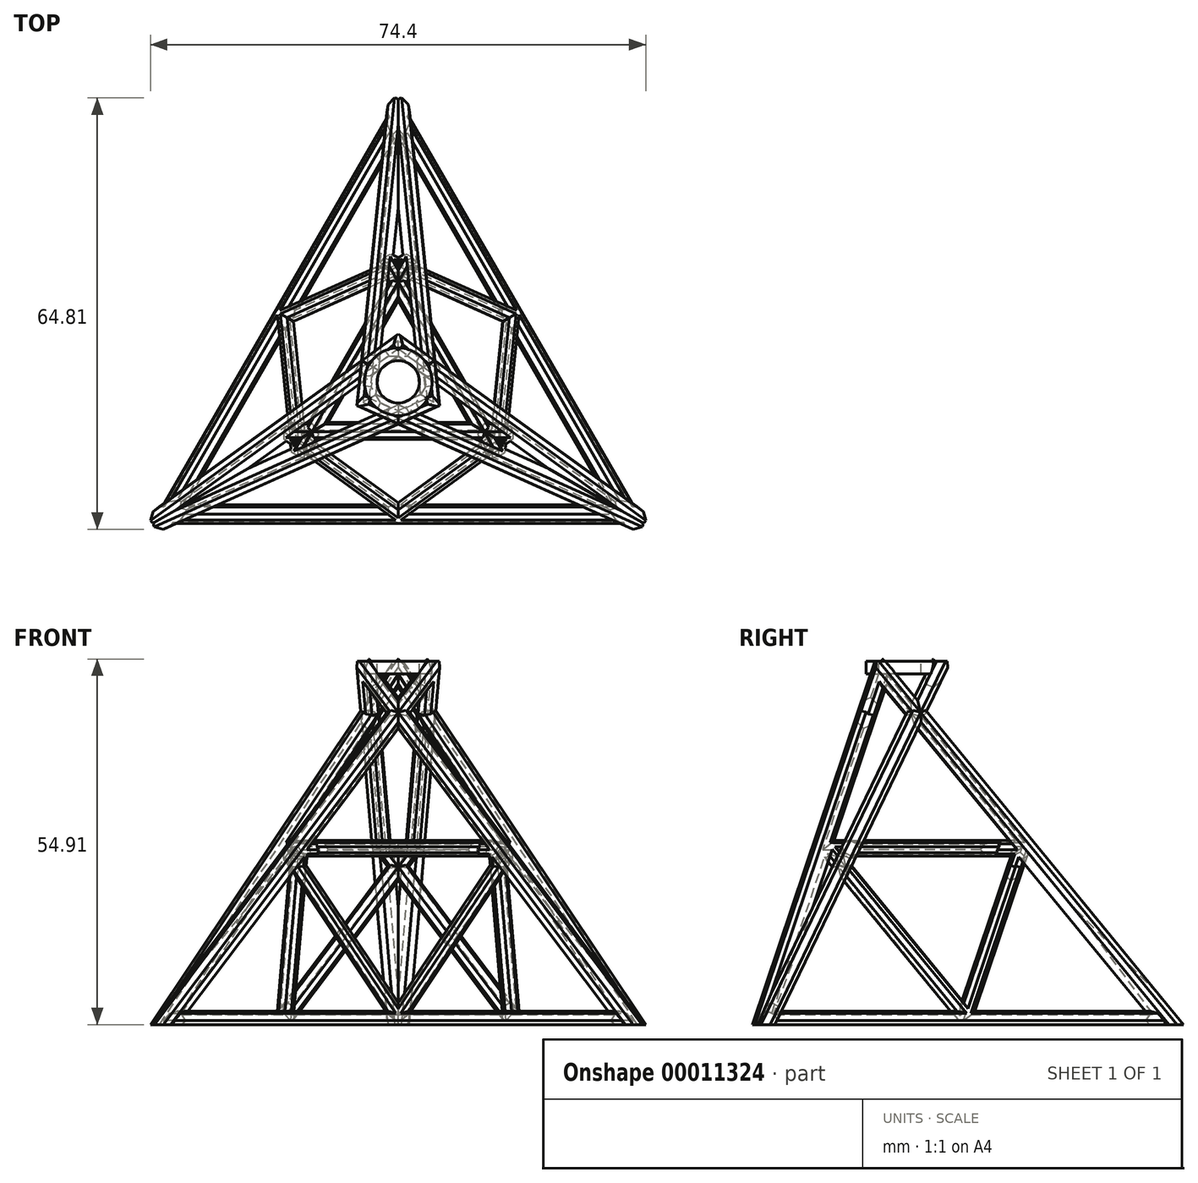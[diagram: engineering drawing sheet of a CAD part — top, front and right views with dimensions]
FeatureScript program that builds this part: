
annotation { "Feature Type Name" : "Feature", "Feature Type Description" : "" }
export const myFeature = defineFeature(function(context is Context, id is Id, definition is map)
    precondition{}
    {
        {
            var Q0;
            Q0=qCreatedBy(makeId("Top.planeOp"),FACE);
            cPlane(context, id + "F0", {"entities" : qUnion([Q0]), "cplaneType" : CPlaneType.OFFSET, "offset" : 38.1 * mm, "width" : 152.4 * mm, "height" : 152.4 * mm});
        }
        {
            var Q0;
            Q0=qCreatedBy(makeId("Front.planeOp"),FACE);
            var sketch = newSketch(context, id + "F1", { "sketchPlane" : qUnion([Q0])});
            skLineSegment(sketch, "E0", {"start": v(0, 0) * mm, "end": v(0, 46.8) * mm, "construction": true});
            skSolve(sketch);
        }
        {
            var Q0;
            Q0=qCreatedBy(id+"F0.planeOp",FACE);
            var sketch = newSketch(context, id + "F2", { "sketchPlane" : qUnion([Q0])});
            skCircle(sketch, "E1", {"center": v(0, 0) * mm, "radius": 3.18 * mm, "construction": true});
            skPoint(sketch, "E2", {"position": v(0, -3.18) * mm});
            skPoint(sketch, "E3.1.0", {"position": v(2.75, -1.59) * mm});
            skPoint(sketch, "E3.2.0", {"position": v(2.75, 1.59) * mm});
            skPoint(sketch, "E3.3.0", {"position": v(0, 3.18) * mm});
            skPoint(sketch, "E3.4.0", {"position": v(-2.75, 1.59) * mm});
            skPoint(sketch, "E3.5.0", {"position": v(-2.75, -1.59) * mm});
            skSolve(sketch);
        }
        {
            var Q0;
            Q0=qCreatedBy(makeId("Top.planeOp"),FACE);
            var sketch = newSketch(context, id + "F3", { "sketchPlane" : qUnion([Q0])});
            skCircle(sketch, "E4", {"center": v(0, 0) * mm, "radius": 21.59 * mm, "construction": true});
            skLineSegment(sketch, "E5", {"start": v(37.4, -21.6) * mm, "end": v(-37.4, -21.59) * mm});
            skLineSegment(sketch, "E6", {"start": v(-37.4, -21.59) * mm, "end": v(0, 43.18) * mm});
            skLineSegment(sketch, "E7", {"start": v(0, 43.18) * mm, "end": v(37.4, -21.6) * mm});
            skPoint(sketch, "E8", {"position": v(0, -21.59) * mm});
            skPoint(sketch, "E9", {"position": v(-18.7, 10.8) * mm});
            skCircle(sketch, "E10", {"center": v(0, 0) * mm, "radius": 38.1 * mm, "construction": true});
            skSolve(sketch);
        }
        {
            var Q0;
            Q0=sQuery(id+"F2.wireOp",VERTEX,"E2");
            var Q1;
            Q1=sQuery(id+"F3.wireOp",VERTEX,"E5.end");
            var Q2;
            Q2=sQuery(id+"F3.wireOp",VERTEX,"E5.start");
            cPlane(context, id + "F4", {"entities" : qUnion([Q0, Q1, Q2]), "cplaneType" : CPlaneType.THREE_POINT, "offset" : 152.4 * mm, "width" : 152.4 * mm, "height" : 152.4 * mm});
        }
        {
            var Q0;
            Q0=qCreatedBy(id+"F4.planeOp",FACE);
            var sketch = newSketch(context, id + "F5", { "sketchPlane" : qUnion([Q0])});
            skPoint(sketch, "E11.0", {"position": v(37.4, -9.4) * mm});
            skPoint(sketch, "E12.0", {"position": v(-37.4, -9.4) * mm});
            skLineSegment(sketch, "E13", {"start": v(37.4, -9.4) * mm, "end": v(0, 52.7) * mm});
            skLineSegment(sketch, "E14", {"start": v(0, 52.7) * mm, "end": v(-37.4, -9.4) * mm});
            skLineSegment(sketch, "E15.0", {"start": v(-37.4, -9.4) * mm, "end": v(37.4, -9.4) * mm});
            skPoint(sketch, "E16", {"position": v(-18.7, 21.65) * mm});
            skPoint(sketch, "E17", {"position": v(18.7, 21.65) * mm});
            skLineSegment(sketch, "E18", {"start": v(-18.7, 21.65) * mm, "end": v(18.7, 21.65) * mm});
            skLineSegment(sketch, "E19", {"start": v(-18.7, 21.65) * mm, "end": v(0, -9.4) * mm});
            skLineSegment(sketch, "E20", {"start": v(0, -9.4) * mm, "end": v(18.7, 21.65) * mm});
            skLineSegment(sketch, "E21.0", {"start": v(32.9, -6.86) * mm, "end": v(0, 47.78) * mm});
            skLineSegment(sketch, "E21.1", {"start": v(-32.9, -6.86) * mm, "end": v(32.9, -6.86) * mm});
            skLineSegment(sketch, "E21.2", {"start": v(0, 47.78) * mm, "end": v(-32.9, -6.86) * mm});
            skLineSegment(sketch, "E22.0", {"start": v(-15.1, 19.62) * mm, "end": v(15.1, 19.62) * mm});
            skLineSegment(sketch, "E22.1", {"start": v(-15.1, 19.62) * mm, "end": v(0, -5.46) * mm});
            skLineSegment(sketch, "E22.2", {"start": v(0, -5.46) * mm, "end": v(15.1, 19.62) * mm});
            skSolve(sketch);
        }
        {
            var Q0;
            {var subQ0=sQuery(id+"F5.wireOp",EDGE,"E21.1");var subQ3=sQuery(id+"F5.wireOp",EDGE,"E21.0");var subQ4=makeQuery(id+"F5.imprint","INTERSECT",VERTEX,{"derivedFrom":[subQ3,subQ0]});Q0=makeQuery(id+"F5.imprint","IMPRINT",FACE,{"disambiguationData":[TD([[makeQuery(id+"F5.imprint","IMPRINT",EDGE,{"disambiguationData":[TD([[subQ4,-1.0]])],"derivedFrom":subQ3}),-1.0]])]});}
            var Q1;
            {var subQ0=sQuery(id+"F5.wireOp",EDGE,"E21.2");var subQ3=sQuery(id+"F5.wireOp",EDGE,"E21.1");var subQ4=makeQuery(id+"F5.imprint","INTERSECT",VERTEX,{"derivedFrom":[subQ3,subQ0]});Q1=makeQuery(id+"F5.imprint","IMPRINT",FACE,{"disambiguationData":[TD([[makeQuery(id+"F5.imprint","IMPRINT",EDGE,{"disambiguationData":[TD([[subQ4,-1.0]])],"derivedFrom":subQ3}),-1.0]])]});}
            var Q2;
            {var subQ0=sQuery(id+"F5.wireOp",EDGE,"E21.0");var subQ3=sQuery(id+"F5.wireOp",EDGE,"E18");var subQ4=makeQuery(id+"F5.imprint","INTERSECT",VERTEX,{"derivedFrom":[subQ3,subQ0]});Q2=makeQuery(id+"F5.imprint","IMPRINT",FACE,{"disambiguationData":[TD([[makeQuery(id+"F5.imprint","IMPRINT",EDGE,{"disambiguationData":[TD([[subQ4,1.0]])],"derivedFrom":subQ0}),-1.0]])]});}
            var Q3;
            {var subQ0=sQuery(id+"F5.wireOp",EDGE,"E21.1");var subQ3=sQuery(id+"F5.wireOp",EDGE,"E19");var subQ4=makeQuery(id+"F5.imprint","INTERSECT",VERTEX,{"derivedFrom":[subQ3,subQ0]});Q3=makeQuery(id+"F5.imprint","IMPRINT",FACE,{"disambiguationData":[TD([[makeQuery(id+"F5.imprint","IMPRINT",EDGE,{"disambiguationData":[TD([[subQ4,-1.0]])],"derivedFrom":subQ0}),-1.0]])]});}
            var Q4;
            Q4=makeQuery(id+"F5.imprint","IMPRINT",FACE,{"disambiguationData":[TD([[makeQuery(id+"F5.imprint","IMPRINT",EDGE,{"derivedFrom":sQuery(id+"F5.wireOp",EDGE,"E22.0")}),1.0]])]});
            var Q5;
            {var subQ0=sQuery(id+"F5.wireOp",EDGE,"E21.2");var subQ3=sQuery(id+"F5.wireOp",EDGE,"E21.0");var subQ4=makeQuery(id+"F5.imprint","INTERSECT",VERTEX,{"derivedFrom":[subQ3,subQ0]});Q5=makeQuery(id+"F5.imprint","IMPRINT",FACE,{"disambiguationData":[TD([[makeQuery(id+"F5.imprint","IMPRINT",EDGE,{"disambiguationData":[TD([[subQ4,1.0]])],"derivedFrom":subQ3}),-1.0]])]});}
            var Q6;
            {var subQ0=sQuery(id+"F5.wireOp",EDGE,"E21.2");var subQ3=sQuery(id+"F5.wireOp",EDGE,"E18");var subQ4=makeQuery(id+"F5.imprint","INTERSECT",VERTEX,{"derivedFrom":[subQ3,subQ0]});Q6=makeQuery(id+"F5.imprint","IMPRINT",FACE,{"disambiguationData":[TD([[makeQuery(id+"F5.imprint","IMPRINT",EDGE,{"disambiguationData":[TD([[subQ4,-1.0]])],"derivedFrom":subQ0}),-1.0]])]});}
            extrude(context, id + "F6", {"entities" : qUnion([Q0, Q1, Q2, Q3, Q4, Q5, Q6]), "depth" : 2.54 * mm});
        }
        {
            var Q0;
            Q0=makeQuery(id+"F6.opExtrude","CAP_EDGE",EDGE,{"disambiguationData":[OSD([sQuery(id+"F5.wireOp",EDGE,"E13")])],"isStart":true});
            var Q1;
            Q1=makeQuery(id+"F6.opExtrude","CAP_EDGE",EDGE,{"disambiguationData":[OSD([sQuery(id+"F5.wireOp",EDGE,"E14")])],"isStart":true});
            var Q2;
            Q2=makeQuery(id+"F6.opExtrude","CAP_EDGE",EDGE,{"disambiguationData":[OSD([sQuery(id+"F5.wireOp",EDGE,"E14")])],"isStart":false});
            var Q3;
            Q3=makeQuery(id+"F6.opExtrude","CAP_EDGE",EDGE,{"disambiguationData":[OSD([sQuery(id+"F5.wireOp",EDGE,"E13")])],"isStart":false});
            var Q4;
            {var subQ0=sQuery(id+"F5.wireOp",EDGE,"E21.0");Q4=makeQuery(id+"F6.opExtrude","CAP_EDGE",EDGE,{"disambiguationData":[OSD([subQ0]),TDD([makeQuery(id+"F5.imprint","IMPRINT",EDGE,{"disambiguationData":[TD([[makeQuery(id+"F5.imprint","INTERSECT",VERTEX,{"derivedFrom":[subQ0,sQuery(id+"F5.wireOp",EDGE,"E21.2")]}),1.0]])],"derivedFrom":subQ0})])],"isStart":true});}
            var Q5;
            {var subQ0=sQuery(id+"F5.wireOp",EDGE,"E21.0");Q5=makeQuery(id+"F6.opExtrude","CAP_EDGE",EDGE,{"disambiguationData":[OSD([subQ0]),TDD([makeQuery(id+"F5.imprint","IMPRINT",EDGE,{"disambiguationData":[TD([[makeQuery(id+"F5.imprint","INTERSECT",VERTEX,{"derivedFrom":[subQ0,sQuery(id+"F5.wireOp",EDGE,"E21.2")]}),1.0]])],"derivedFrom":subQ0})])],"isStart":false});}
            var Q6;
            {var subQ0=sQuery(id+"F5.wireOp",EDGE,"E21.2");Q6=makeQuery(id+"F6.opExtrude","CAP_EDGE",EDGE,{"disambiguationData":[OSD([subQ0]),TDD([makeQuery(id+"F5.imprint","IMPRINT",EDGE,{"disambiguationData":[TD([[makeQuery(id+"F5.imprint","INTERSECT",VERTEX,{"derivedFrom":[sQuery(id+"F5.wireOp",EDGE,"E21.0"),subQ0]}),-1.0]])],"derivedFrom":subQ0})])],"isStart":true});}
            var Q7;
            {var subQ0=sQuery(id+"F5.wireOp",EDGE,"E21.2");Q7=makeQuery(id+"F6.opExtrude","CAP_EDGE",EDGE,{"disambiguationData":[OSD([subQ0]),TDD([makeQuery(id+"F5.imprint","IMPRINT",EDGE,{"disambiguationData":[TD([[makeQuery(id+"F5.imprint","INTERSECT",VERTEX,{"derivedFrom":[sQuery(id+"F5.wireOp",EDGE,"E21.0"),subQ0]}),-1.0]])],"derivedFrom":subQ0})])],"isStart":false});}
            var Q8;
            Q8=makeQuery(id+"F6.opExtrude","CAP_EDGE",EDGE,{"disambiguationData":[OSD([sQuery(id+"F5.wireOp",EDGE,"E18")])],"isStart":true});
            var Q9;
            Q9=makeQuery(id+"F6.opExtrude","CAP_EDGE",EDGE,{"disambiguationData":[OSD([sQuery(id+"F5.wireOp",EDGE,"E18")])],"isStart":false});
            var Q10;
            Q10=makeQuery(id+"F6.opExtrude","CAP_EDGE",EDGE,{"disambiguationData":[OSD([sQuery(id+"F5.wireOp",EDGE,"E22.0")])],"isStart":true});
            var Q11;
            Q11=makeQuery(id+"F6.opExtrude","CAP_EDGE",EDGE,{"disambiguationData":[OSD([sQuery(id+"F5.wireOp",EDGE,"E22.0")])],"isStart":false});
            var Q12;
            Q12=makeQuery(id+"F6.opExtrude","CAP_EDGE",EDGE,{"disambiguationData":[OSD([sQuery(id+"F5.wireOp",EDGE,"E22.2")])],"isStart":true});
            var Q13;
            Q13=makeQuery(id+"F6.opExtrude","CAP_EDGE",EDGE,{"disambiguationData":[OSD([sQuery(id+"F5.wireOp",EDGE,"E22.2")])],"isStart":false});
            var Q14;
            Q14=makeQuery(id+"F6.opExtrude","CAP_EDGE",EDGE,{"disambiguationData":[OSD([sQuery(id+"F5.wireOp",EDGE,"E22.1")])],"isStart":true});
            var Q15;
            Q15=makeQuery(id+"F6.opExtrude","CAP_EDGE",EDGE,{"disambiguationData":[OSD([sQuery(id+"F5.wireOp",EDGE,"E19")])],"isStart":true});
            var Q16;
            Q16=makeQuery(id+"F6.opExtrude","CAP_EDGE",EDGE,{"disambiguationData":[OSD([sQuery(id+"F5.wireOp",EDGE,"E19")])],"isStart":false});
            var Q17;
            Q17=makeQuery(id+"F6.opExtrude","CAP_EDGE",EDGE,{"disambiguationData":[OSD([sQuery(id+"F5.wireOp",EDGE,"E22.1")])],"isStart":false});
            var Q18;
            Q18=makeQuery(id+"F6.opExtrude","CAP_EDGE",EDGE,{"disambiguationData":[OSD([sQuery(id+"F5.wireOp",EDGE,"E20")])],"isStart":false});
            var Q19;
            Q19=makeQuery(id+"F6.opExtrude","CAP_EDGE",EDGE,{"disambiguationData":[OSD([sQuery(id+"F5.wireOp",EDGE,"E20")])],"isStart":true});
            var Q20;
            {var subQ0=sQuery(id+"F5.wireOp",EDGE,"E21.1");Q20=makeQuery(id+"F6.opExtrude","CAP_EDGE",EDGE,{"disambiguationData":[OSD([subQ0]),TDD([makeQuery(id+"F5.imprint","IMPRINT",EDGE,{"disambiguationData":[TD([[makeQuery(id+"F5.imprint","INTERSECT",VERTEX,{"derivedFrom":[sQuery(id+"F5.wireOp",EDGE,"E21.0"),subQ0]}),1.0]])],"derivedFrom":subQ0})])],"isStart":false});}
            var Q21;
            {var subQ0=sQuery(id+"F5.wireOp",EDGE,"E21.1");Q21=makeQuery(id+"F6.opExtrude","CAP_EDGE",EDGE,{"disambiguationData":[OSD([subQ0]),TDD([makeQuery(id+"F5.imprint","IMPRINT",EDGE,{"disambiguationData":[TD([[makeQuery(id+"F5.imprint","INTERSECT",VERTEX,{"derivedFrom":[sQuery(id+"F5.wireOp",EDGE,"E21.0"),subQ0]}),1.0]])],"derivedFrom":subQ0})])],"isStart":true});}
            var Q22;
            {var subQ0=sQuery(id+"F5.wireOp",EDGE,"E21.1");Q22=makeQuery(id+"F6.opExtrude","CAP_EDGE",EDGE,{"disambiguationData":[OSD([subQ0]),TDD([makeQuery(id+"F5.imprint","IMPRINT",EDGE,{"disambiguationData":[TD([[makeQuery(id+"F5.imprint","INTERSECT",VERTEX,{"derivedFrom":[subQ0,sQuery(id+"F5.wireOp",EDGE,"E21.2")]}),-1.0]])],"derivedFrom":subQ0})])],"isStart":false});}
            var Q23;
            {var subQ0=sQuery(id+"F5.wireOp",EDGE,"E21.1");Q23=makeQuery(id+"F6.opExtrude","CAP_EDGE",EDGE,{"disambiguationData":[OSD([subQ0]),TDD([makeQuery(id+"F5.imprint","IMPRINT",EDGE,{"disambiguationData":[TD([[makeQuery(id+"F5.imprint","INTERSECT",VERTEX,{"derivedFrom":[subQ0,sQuery(id+"F5.wireOp",EDGE,"E21.2")]}),-1.0]])],"derivedFrom":subQ0})])],"isStart":true});}
            var Q24;
            Q24=makeQuery(id+"F6.opExtrude","CAP_EDGE",EDGE,{"disambiguationData":[OSD([sQuery(id+"F5.wireOp",EDGE,"E15.0")])],"isStart":true});
            chamfer(context, id + "F7", {"entities" : qUnion([Q0, Q1, Q2, Q3, Q4, Q5, Q6, Q7, Q8, Q9, Q10, Q11, Q12, Q13, Q14, Q15, Q16, Q17, Q18, Q19, Q20, Q21, Q22, Q23, Q24]), "width" : 0.66 * mm, "tangentPropagation" : true});
        }
        {
            var Q0;
            Q0=makeQuery(id+"F6.opExtrude","SWEPT_BODY",BODY,{"disambiguationData":[OSD([sQuery(id+"F5.wireOp",EDGE,"E13"),sQuery(id+"F5.wireOp",EDGE,"E14"),sQuery(id+"F5.wireOp",EDGE,"E15.0"),sQuery(id+"F5.wireOp",EDGE,"E18"),sQuery(id+"F5.wireOp",EDGE,"E19"),sQuery(id+"F5.wireOp",EDGE,"E20"),sQuery(id+"F5.wireOp",EDGE,"E21.0"),sQuery(id+"F5.wireOp",EDGE,"E21.1"),sQuery(id+"F5.wireOp",EDGE,"E21.2"),sQuery(id+"F5.wireOp",EDGE,"E22.0"),sQuery(id+"F5.wireOp",EDGE,"E22.1"),sQuery(id+"F5.wireOp",EDGE,"E22.2")])]});
            var Q1;
            Q1=sQuery(id+"F1.wireOp",EDGE,"E0");
            circularPattern(context, id + "F8", {"operationType" : NewBodyOperationType.ADD, "entities" : qUnion([Q0]), "axis" : qUnion([Q1]), "angle" : 120 * degree, "instanceCount" : 3});
        }
        {
            var Q0;
            Q0=qCreatedBy(makeId("Top.planeOp"),FACE);
            cPlane(context, id + "F9", {"entities" : qUnion([Q0]), "cplaneType" : CPlaneType.OFFSET, "offset" : 54.6 * mm, "width" : 152.4 * mm, "height" : 152.4 * mm});
        }
        {
            var Q0;
            Q0=qCreatedBy(id+"F9.planeOp",FACE);
            var sketch = newSketch(context, id + "F10", { "sketchPlane" : qUnion([Q0])});
            skCircle(sketch, "E23.0", {"center": v(0, 0) * mm, "radius": 3.18 * mm});
            skPoint(sketch, "E24.0", {"position": v(0, -3.18) * mm});
            skCircle(sketch, "E25.0", {"center": v(0, 0) * mm, "radius": 5.08 * mm});
            skCircle(sketch, "E26", {"center": v(0, 0) * mm, "radius": 4.76 * mm, "construction": true});
            skLineSegment(sketch, "E27.rect.bottom", {"start": v(12.7, 12.7) * mm, "end": v(-12.7, 12.7) * mm});
            skLineSegment(sketch, "E27.rect.top", {"start": v(12.7, -12.7) * mm, "end": v(-12.7, -12.7) * mm});
            skLineSegment(sketch, "E27.rect.left", {"start": v(12.7, 12.7) * mm, "end": v(12.7, -12.7) * mm});
            skLineSegment(sketch, "E27.rect.right", {"start": v(-12.7, 12.7) * mm, "end": v(-12.7, -12.7) * mm});
            skSolve(sketch);
        }
        {
            var Q0;
            Q0=makeQuery(id+"F10.imprint","IMPRINT",FACE,{"disambiguationData":[TD([[makeQuery(id+"F10.imprint","IMPRINT",EDGE,{"derivedFrom":sQuery(id+"F10.wireOp",EDGE,"E23.0")}),-1.0]])]});
            extrude(context, id + "F11", {"entities" : qUnion([Q0]), "operationType" : NewBodyOperationType.ADD, "oppositeDirection" : true, "depth" : 1.9 * mm});
        }
        {
            var Q0;
            Q0=qCreatedBy(makeId("Top.planeOp"),FACE);
            var sketch = newSketch(context, id + "F12", { "sketchPlane" : qUnion([Q0])});
            skLineSegment(sketch, "E28.rect.bottom", {"start": v(45.95, -48.28) * mm, "end": v(-45.95, -48.28) * mm});
            skLineSegment(sketch, "E28.rect.top", {"start": v(45.95, 48.28) * mm, "end": v(-45.95, 48.28) * mm});
            skLineSegment(sketch, "E28.rect.left", {"start": v(45.95, -48.28) * mm, "end": v(45.95, 48.28) * mm});
            skLineSegment(sketch, "E28.rect.right", {"start": v(-45.95, -48.28) * mm, "end": v(-45.95, 48.28) * mm});
            skPoint(sketch, "E28.rect.middle", {"position": v(0, 0) * mm});
            skSolve(sketch);
        }
        {
            var Q0;
            Q0=makeQuery(id+"F12.imprint","IMPRINT",FACE,{"disambiguationData":[TD([[makeQuery(id+"F12.imprint","IMPRINT",EDGE,{"derivedFrom":sQuery(id+"F12.wireOp",EDGE,"E28.rect.bottom")}),-1.0]])]});
            extrude(context, id + "F13", {"entities" : qUnion([Q0]), "operationType" : NewBodyOperationType.REMOVE, "oppositeDirection" : true, "depth" : 25.4 * mm});
        }
        {
            var Q0;
            Q0=makeQuery(id+"F10.imprint","IMPRINT",FACE,{"disambiguationData":[TD([[makeQuery(id+"F10.imprint","IMPRINT",EDGE,{"derivedFrom":sQuery(id+"F10.wireOp",EDGE,"E25.0")}),-1.0]])]});
            extrude(context, id + "F14", {"entities" : qUnion([Q0]), "operationType" : NewBodyOperationType.REMOVE, "depth" : 25.4 * mm});
        }
    });
